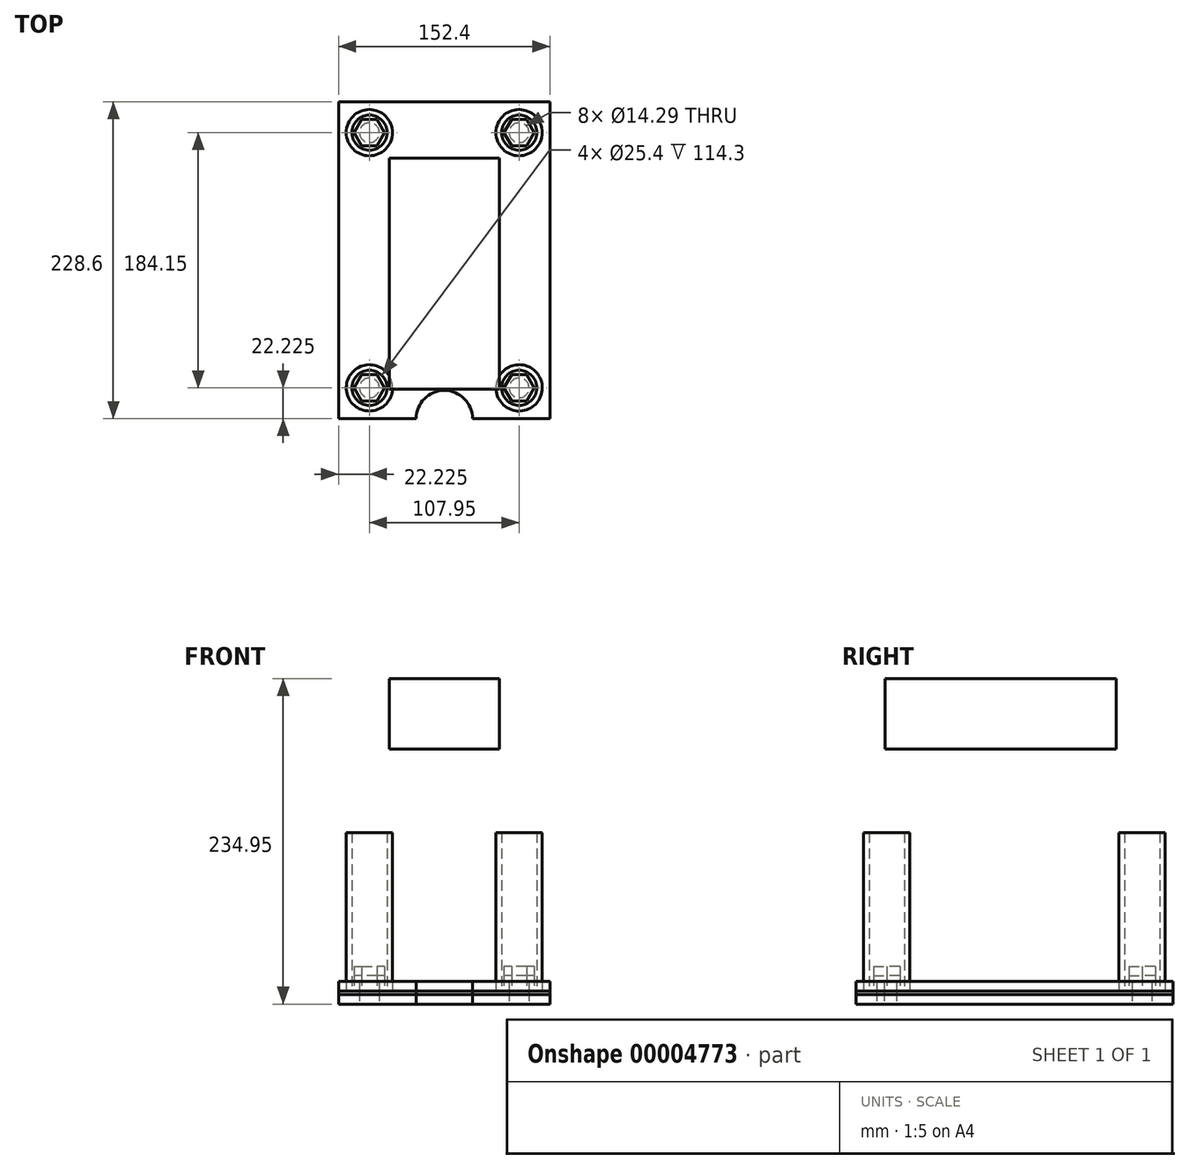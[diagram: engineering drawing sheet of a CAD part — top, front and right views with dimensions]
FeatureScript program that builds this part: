
annotation { "Feature Type Name" : "Feature", "Feature Type Description" : "" }
export const myFeature = defineFeature(function(context is Context, id is Id, definition is map)
    precondition{}
    {
        {
            var Q0;
            Q0=qCreatedBy(makeId("Top.planeOp"),FACE);
            var sketch = newSketch(context, id + "F0", { "sketchPlane" : qUnion([Q0])});
            skLineSegment(sketch, "E0.bottom", {"start": v(0, 228.6) * mm, "end": v(152.4, 228.6) * mm});
            skLineSegment(sketch, "E0.top", {"start": v(0, 0) * mm, "end": v(152.4, 0) * mm});
            skLineSegment(sketch, "E0.left", {"start": v(0, 228.6) * mm, "end": v(0, 0) * mm});
            skLineSegment(sketch, "E0.right", {"start": v(152.4, 228.6) * mm, "end": v(152.4, 0) * mm});
            skCircle(sketch, "E1", {"center": v(76.2, 0) * mm, "radius": 20.32 * mm});
            skLineSegment(sketch, "E2.bottom", {"start": v(36.51, 187.93) * mm, "end": v(115.89, 187.93) * mm});
            skLineSegment(sketch, "E2.top", {"start": v(36.51, 21.24) * mm, "end": v(115.89, 21.24) * mm});
            skLineSegment(sketch, "E2.left", {"start": v(36.51, 187.93) * mm, "end": v(36.51, 21.24) * mm});
            skLineSegment(sketch, "E2.right", {"start": v(115.89, 187.93) * mm, "end": v(115.89, 21.24) * mm});
            skSolve(sketch);
        }
        {
            var Q0;
            Q0=qCreatedBy(makeId("Top.planeOp"),FACE);
            var sketch = newSketch(context, id + "F1", { "sketchPlane" : qUnion([Q0])});
            skCircle(sketch, "E3", {"center": v(22.22, 22.22) * mm, "radius": 7.14 * mm});
            skCircle(sketch, "E4.0.1.0", {"center": v(22.22, 206.38) * mm, "radius": 7.14 * mm});
            skCircle(sketch, "E4.1.0.0", {"center": v(130.17, 22.22) * mm, "radius": 7.14 * mm});
            skCircle(sketch, "E4.1.1.0", {"center": v(130.17, 206.38) * mm, "radius": 7.14 * mm});
            skLineSegment(sketch, "E4.direction1", {"start": v(22.22, 22.22) * mm, "end": v(130.17, 22.22) * mm, "construction": true});
            skLineSegment(sketch, "E4.direction2", {"start": v(22.22, 22.22) * mm, "end": v(22.22, 206.38) * mm, "construction": true});
            skSolve(sketch);
        }
        {
            var Q0;
            Q0=makeQuery(id+"F0.imprint","IMPRINT",FACE,{"disambiguationData":[TD([[makeQuery(id+"F0.imprint","IMPRINT",EDGE,{"derivedFrom":sQuery(id+"F0.wireOp",EDGE,"E0.bottom")}),-1.0]])]});
            var Q1;
            Q1=makeQuery(id+"F0.imprint","IMPRINT",FACE,{"disambiguationData":[TD([[makeQuery(id+"F0.imprint","IMPRINT",EDGE,{"derivedFrom":sQuery(id+"F0.wireOp",EDGE,"E2.bottom")}),-1.0]])]});
            extrude(context, id + "F2", {"entities" : qUnion([Q0, Q1]), "depth" : 9.52 * mm, "offsetDistance" : 25.4 * mm});
        }
        {
            var Q0;
            Q0=makeQuery(id+"F0.imprint","IMPRINT",FACE,{"disambiguationData":[TD([[makeQuery(id+"F0.imprint","IMPRINT",EDGE,{"derivedFrom":sQuery(id+"F0.wireOp",EDGE,"E2.bottom")}),-1.0]])]});
            extrude(context, id + "F3", {"entities" : qUnion([Q0]), "depth" : 50.8 * mm, "offsetDistance" : 25.4 * mm});
        }
        {
            var Q0;
            Q0 = qSketchRegion(id + "F1", true);
            extrude(context, id + "F4", {"entities" : qUnion([Q0]), "operationType" : NewBodyOperationType.REMOVE, "endBound" : BoundingType.SYMMETRIC, "depth" : 25.4 * mm, "offsetDistance" : 25.4 * mm});
        }
        {
            var Q0;
            Q0=qCreatedBy(makeId("Top.planeOp"),FACE);
            var sketch = newSketch(context, id + "F5", { "sketchPlane" : qUnion([Q0])});
            skCircle(sketch, "E5.cCircle", {"center": v(22.22, 22.22) * mm, "radius": 9.53 * mm, "construction": true});
            skLineSegment(sketch, "E5.0", {"start": v(33.22, 22.22) * mm, "end": v(27.72, 12.7) * mm});
            skLineSegment(sketch, "E5.1", {"start": v(27.72, 12.7) * mm, "end": v(16.73, 12.7) * mm});
            skLineSegment(sketch, "E5.2", {"start": v(16.73, 12.7) * mm, "end": v(11.23, 22.23) * mm});
            skLineSegment(sketch, "E5.3", {"start": v(11.23, 22.23) * mm, "end": v(16.73, 31.75) * mm});
            skLineSegment(sketch, "E5.4", {"start": v(16.73, 31.75) * mm, "end": v(27.72, 31.75) * mm});
            skLineSegment(sketch, "E5.5", {"start": v(27.72, 31.75) * mm, "end": v(33.22, 22.22) * mm});
            skPoint(sketch, "E5.0.midPoint", {"position": v(30.47, 17.46) * mm});
            skLineSegment(sketch, "E6.0.1.0", {"start": v(27.72, 196.85) * mm, "end": v(16.73, 196.85) * mm});
            skLineSegment(sketch, "E6.0.1.1", {"start": v(16.73, 196.85) * mm, "end": v(11.23, 206.38) * mm});
            skCircle(sketch, "E6.0.1.2", {"center": v(22.22, 206.38) * mm, "radius": 9.53 * mm, "construction": true});
            skPoint(sketch, "E6.0.1.3", {"position": v(30.47, 201.61) * mm});
            skLineSegment(sketch, "E6.0.1.4", {"start": v(33.22, 206.38) * mm, "end": v(27.72, 196.85) * mm});
            skLineSegment(sketch, "E6.0.1.5", {"start": v(16.73, 215.9) * mm, "end": v(27.72, 215.9) * mm});
            skLineSegment(sketch, "E6.0.1.6", {"start": v(11.23, 206.38) * mm, "end": v(16.73, 215.9) * mm});
            skLineSegment(sketch, "E6.0.1.7", {"start": v(27.72, 215.9) * mm, "end": v(33.22, 206.38) * mm});
            skLineSegment(sketch, "E6.1.0.0", {"start": v(135.67, 12.7) * mm, "end": v(124.68, 12.7) * mm});
            skLineSegment(sketch, "E6.1.0.1", {"start": v(124.68, 12.7) * mm, "end": v(119.18, 22.22) * mm});
            skCircle(sketch, "E6.1.0.2", {"center": v(130.17, 22.22) * mm, "radius": 9.53 * mm, "construction": true});
            skPoint(sketch, "E6.1.0.3", {"position": v(138.42, 17.46) * mm});
            skLineSegment(sketch, "E6.1.0.4", {"start": v(141.17, 22.22) * mm, "end": v(135.67, 12.7) * mm});
            skLineSegment(sketch, "E6.1.0.5", {"start": v(124.68, 31.75) * mm, "end": v(135.67, 31.75) * mm});
            skLineSegment(sketch, "E6.1.0.6", {"start": v(119.18, 22.23) * mm, "end": v(124.68, 31.75) * mm});
            skLineSegment(sketch, "E6.1.0.7", {"start": v(135.67, 31.75) * mm, "end": v(141.17, 22.22) * mm});
            skLineSegment(sketch, "E6.1.1.0", {"start": v(135.67, 196.85) * mm, "end": v(124.68, 196.85) * mm});
            skLineSegment(sketch, "E6.1.1.1", {"start": v(124.68, 196.85) * mm, "end": v(119.18, 206.38) * mm});
            skCircle(sketch, "E6.1.1.2", {"center": v(130.17, 206.38) * mm, "radius": 9.53 * mm, "construction": true});
            skPoint(sketch, "E6.1.1.3", {"position": v(138.42, 201.61) * mm});
            skLineSegment(sketch, "E6.1.1.4", {"start": v(141.17, 206.38) * mm, "end": v(135.67, 196.85) * mm});
            skLineSegment(sketch, "E6.1.1.5", {"start": v(124.68, 215.9) * mm, "end": v(135.67, 215.9) * mm});
            skLineSegment(sketch, "E6.1.1.6", {"start": v(119.18, 206.38) * mm, "end": v(124.68, 215.9) * mm});
            skLineSegment(sketch, "E6.1.1.7", {"start": v(135.67, 215.9) * mm, "end": v(141.17, 206.38) * mm});
            skLineSegment(sketch, "E6.direction1", {"start": v(22.22, 22.22) * mm, "end": v(130.18, 22.22) * mm, "construction": true});
            skLineSegment(sketch, "E6.direction2", {"start": v(22.22, 22.22) * mm, "end": v(22.22, 206.38) * mm, "construction": true});
            skSolve(sketch);
        }
        {
            var Q0;
            Q0=makeQuery(id+"F2.opExtrude","SWEPT_BODY",BODY,{"disambiguationData":[OSD([sQuery(id+"F0.wireOp",EDGE,"E0.bottom"),sQuery(id+"F0.wireOp",EDGE,"E0.top"),sQuery(id+"F0.wireOp",EDGE,"E0.left"),sQuery(id+"F0.wireOp",EDGE,"E0.right"),sQuery(id+"F0.wireOp",EDGE,"E1")])]});
            transform(context, id + "F6", {"entities" : qUnion([Q0]), "transformType" : TransformType.TRANSLATION_3D, "dx" : 0 * mm, "dy" : 0 * mm, "dz" : (6 + (5 / 8) + .25) * mm, "makeCopy" : true});
        }
        {
            var Q0;
            Q0 = qSketchRegion(id + "F5", true);
            extrude(context, id + "F7", {"entities" : qUnion([Q0]), "depth" : 11.1 * mm, "offsetDistance" : 25.4 * mm});
        }
        {
            var Q0;
            Q0=makeQuery(id+"F7.opExtrude","SWEPT_BODY",BODY,{"disambiguationData":[OSD([sQuery(id+"F5.wireOp",EDGE,"E5.0"),sQuery(id+"F5.wireOp",EDGE,"E5.1"),sQuery(id+"F5.wireOp",EDGE,"E5.2"),sQuery(id+"F5.wireOp",EDGE,"E5.3"),sQuery(id+"F5.wireOp",EDGE,"E5.4"),sQuery(id+"F5.wireOp",EDGE,"E5.5")])]});
            var Q1;
            Q1=makeQuery(id+"F7.opExtrude","SWEPT_BODY",BODY,{"disambiguationData":[OSD([sQuery(id+"F5.wireOp",EDGE,"E6.0.1.0"),sQuery(id+"F5.wireOp",EDGE,"E6.0.1.1"),sQuery(id+"F5.wireOp",EDGE,"E6.0.1.4"),sQuery(id+"F5.wireOp",EDGE,"E6.0.1.5"),sQuery(id+"F5.wireOp",EDGE,"E6.0.1.6"),sQuery(id+"F5.wireOp",EDGE,"E6.0.1.7")])]});
            var Q2;
            Q2=makeQuery(id+"F7.opExtrude","SWEPT_BODY",BODY,{"disambiguationData":[OSD([sQuery(id+"F5.wireOp",EDGE,"E6.1.0.0"),sQuery(id+"F5.wireOp",EDGE,"E6.1.0.1"),sQuery(id+"F5.wireOp",EDGE,"E6.1.0.4"),sQuery(id+"F5.wireOp",EDGE,"E6.1.0.5"),sQuery(id+"F5.wireOp",EDGE,"E6.1.0.6"),sQuery(id+"F5.wireOp",EDGE,"E6.1.0.7")])]});
            var Q3;
            Q3=makeQuery(id+"F7.opExtrude","SWEPT_BODY",BODY,{"disambiguationData":[OSD([sQuery(id+"F5.wireOp",EDGE,"E6.1.1.0"),sQuery(id+"F5.wireOp",EDGE,"E6.1.1.1"),sQuery(id+"F5.wireOp",EDGE,"E6.1.1.4"),sQuery(id+"F5.wireOp",EDGE,"E6.1.1.5"),sQuery(id+"F5.wireOp",EDGE,"E6.1.1.6"),sQuery(id+"F5.wireOp",EDGE,"E6.1.1.7")])]});
            transform(context, id + "F8", {"entities" : qUnion([Q0, Q1, Q2, Q3]), "transformType" : TransformType.TRANSLATION_3D, "dx" : 0 * mm, "dy" : 0 * mm, "dz" : 9.52 * mm, "makeCopy" : false});
        }
        {
            var Q0;
            Q0=makeQuery(id+"F7.opExtrude","SWEPT_BODY",BODY,{"disambiguationData":[OSD([sQuery(id+"F5.wireOp",EDGE,"E5.0"),sQuery(id+"F5.wireOp",EDGE,"E5.1"),sQuery(id+"F5.wireOp",EDGE,"E5.2"),sQuery(id+"F5.wireOp",EDGE,"E5.3"),sQuery(id+"F5.wireOp",EDGE,"E5.4"),sQuery(id+"F5.wireOp",EDGE,"E5.5")])]});
            var Q1;
            Q1=makeQuery(id+"F7.opExtrude","SWEPT_BODY",BODY,{"disambiguationData":[OSD([sQuery(id+"F5.wireOp",EDGE,"E6.0.1.0"),sQuery(id+"F5.wireOp",EDGE,"E6.0.1.1"),sQuery(id+"F5.wireOp",EDGE,"E6.0.1.4"),sQuery(id+"F5.wireOp",EDGE,"E6.0.1.5"),sQuery(id+"F5.wireOp",EDGE,"E6.0.1.6"),sQuery(id+"F5.wireOp",EDGE,"E6.0.1.7")])]});
            var Q2;
            Q2=makeQuery(id+"F7.opExtrude","SWEPT_BODY",BODY,{"disambiguationData":[OSD([sQuery(id+"F5.wireOp",EDGE,"E6.1.0.0"),sQuery(id+"F5.wireOp",EDGE,"E6.1.0.1"),sQuery(id+"F5.wireOp",EDGE,"E6.1.0.4"),sQuery(id+"F5.wireOp",EDGE,"E6.1.0.5"),sQuery(id+"F5.wireOp",EDGE,"E6.1.0.6"),sQuery(id+"F5.wireOp",EDGE,"E6.1.0.7")])]});
            var Q3;
            Q3=makeQuery(id+"F7.opExtrude","SWEPT_BODY",BODY,{"disambiguationData":[OSD([sQuery(id+"F5.wireOp",EDGE,"E6.1.1.0"),sQuery(id+"F5.wireOp",EDGE,"E6.1.1.1"),sQuery(id+"F5.wireOp",EDGE,"E6.1.1.4"),sQuery(id+"F5.wireOp",EDGE,"E6.1.1.5"),sQuery(id+"F5.wireOp",EDGE,"E6.1.1.6"),sQuery(id+"F5.wireOp",EDGE,"E6.1.1.7")])]});
            transform(context, id + "F9", {"entities" : qUnion([Q0, Q1, Q2, Q3]), "transformType" : TransformType.TRANSLATION_3D, "dx" : 0 * mm, "dy" : 0 * mm, "dz" : (6 + (7 / 16)) * mm, "makeCopy" : true});
        }
        {
            var Q0;
            Q0=makeQuery(id+"F3.opExtrude","SWEPT_BODY",BODY,{"disambiguationData":[OSD([sQuery(id+"F0.wireOp",EDGE,"E2.bottom"),sQuery(id+"F0.wireOp",EDGE,"E2.top"),sQuery(id+"F0.wireOp",EDGE,"E2.left"),sQuery(id+"F0.wireOp",EDGE,"E2.right")])]});
            transform(context, id + "F10", {"entities" : qUnion([Q0]), "transformType" : TransformType.TRANSLATION_3D, "dx" : 0 * mm, "dy" : 0 * mm, "dz" : 184.15 * mm, "makeCopy" : false});
        }
        {
            var Q0;
            Q0=qCreatedBy(makeId("Top.planeOp"),FACE);
            var sketch = newSketch(context, id + "F11", { "sketchPlane" : qUnion([Q0])});
            skCircle(sketch, "E7", {"center": v(22.22, 22.22) * mm, "radius": 16.7 * mm});
            skCircle(sketch, "E8", {"center": v(22.22, 22.22) * mm, "radius": 12.7 * mm});
            skCircle(sketch, "E9.0.1.0", {"center": v(22.22, 206.38) * mm, "radius": 16.7 * mm});
            skCircle(sketch, "E9.0.1.1", {"center": v(22.22, 206.38) * mm, "radius": 12.7 * mm});
            skCircle(sketch, "E9.1.0.0", {"center": v(130.17, 22.22) * mm, "radius": 16.7 * mm});
            skCircle(sketch, "E9.1.0.1", {"center": v(130.17, 22.22) * mm, "radius": 12.7 * mm});
            skCircle(sketch, "E9.1.1.0", {"center": v(130.17, 206.38) * mm, "radius": 16.7 * mm});
            skCircle(sketch, "E9.1.1.1", {"center": v(130.17, 206.38) * mm, "radius": 12.7 * mm});
            skLineSegment(sketch, "E9.direction1", {"start": v(22.22, 22.22) * mm, "end": v(130.17, 22.22) * mm, "construction": true});
            skLineSegment(sketch, "E9.direction2", {"start": v(22.22, 22.22) * mm, "end": v(22.22, 206.38) * mm, "construction": true});
            skSolve(sketch);
        }
        {
            var Q0;
            Q0=makeQuery(id+"F11.imprint","IMPRINT",FACE,{"disambiguationData":[TD([[makeQuery(id+"F11.imprint","IMPRINT",EDGE,{"derivedFrom":sQuery(id+"F11.wireOp",EDGE,"E9.0.1.0")}),1.0]])]});
            var Q1;
            Q1=makeQuery(id+"F11.imprint","IMPRINT",FACE,{"disambiguationData":[TD([[makeQuery(id+"F11.imprint","IMPRINT",EDGE,{"derivedFrom":sQuery(id+"F11.wireOp",EDGE,"E9.1.1.0")}),1.0]])]});
            var Q2;
            Q2=makeQuery(id+"F11.imprint","IMPRINT",FACE,{"disambiguationData":[TD([[makeQuery(id+"F11.imprint","IMPRINT",EDGE,{"derivedFrom":sQuery(id+"F11.wireOp",EDGE,"E9.1.0.0")}),1.0]])]});
            var Q3;
            Q3=makeQuery(id+"F11.imprint","IMPRINT",FACE,{"disambiguationData":[TD([[makeQuery(id+"F11.imprint","IMPRINT",EDGE,{"derivedFrom":sQuery(id+"F11.wireOp",EDGE,"E7")}),1.0]])]});
            extrude(context, id + "F12", {"entities" : qUnion([Q0, Q1, Q2, Q3]), "depth" : 114.3 * mm, "offsetDistance" : 25.4 * mm});
        }
        {
            var Q0;
            Q0=makeQuery(id+"F12.opExtrude","SWEPT_BODY",BODY,{"disambiguationData":[OSD([sQuery(id+"F11.wireOp",EDGE,"E9.1.1.0"),sQuery(id+"F11.wireOp",EDGE,"E9.1.1.1")])]});
            var Q1;
            Q1=makeQuery(id+"F12.opExtrude","SWEPT_BODY",BODY,{"disambiguationData":[OSD([sQuery(id+"F11.wireOp",EDGE,"E7"),sQuery(id+"F11.wireOp",EDGE,"E8")])]});
            var Q2;
            Q2=makeQuery(id+"F12.opExtrude","SWEPT_BODY",BODY,{"disambiguationData":[OSD([sQuery(id+"F11.wireOp",EDGE,"E9.0.1.0"),sQuery(id+"F11.wireOp",EDGE,"E9.0.1.1")])]});
            var Q3;
            Q3=makeQuery(id+"F12.opExtrude","SWEPT_BODY",BODY,{"disambiguationData":[OSD([sQuery(id+"F11.wireOp",EDGE,"E9.1.0.0"),sQuery(id+"F11.wireOp",EDGE,"E9.1.0.1")])]});
            transform(context, id + "F13", {"entities" : qUnion([Q0, Q1, Q2, Q3]), "transformType" : TransformType.TRANSLATION_3D, "dx" : 0 * mm, "dy" : 0 * mm, "dz" : 9.52 * mm, "makeCopy" : false});
        }
    });
